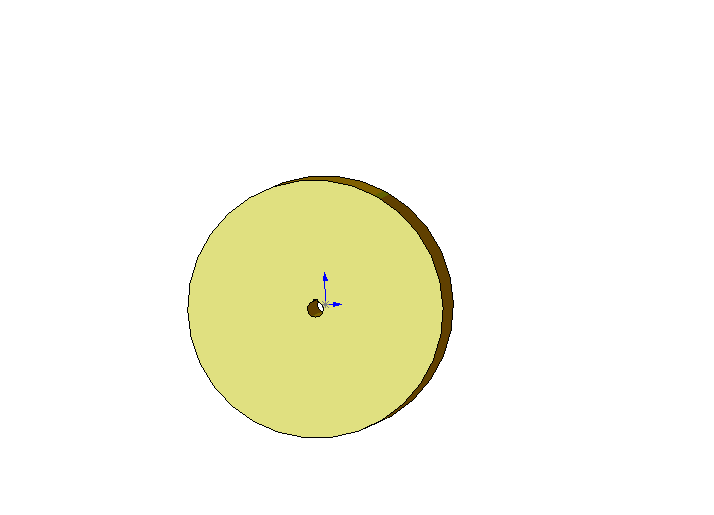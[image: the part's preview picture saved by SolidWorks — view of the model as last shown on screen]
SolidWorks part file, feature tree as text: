
SOLIDWORKS PART (.sldprt)
format: sldprt  version: not decoded by parser v0  size: 113,152 bytes
history: native  units: mm
features: sketch x3, cut_extrude x2, extrude x1 (+10 scaffold rows collapsed)
feature tree (16):
  scaffold x10  (default folders/planes/origin — collapsed)
  sketch  "Sketch1"  dims[D1=203.2mm]
  extrude  "Extrude1"  Depth=50.8mm
  sketch  "Sketch2"  dims[D1=12.7mm]
  cut_extrude  "Cut-Extrude1"  Depth=50.8mm
  sketch  "Sketch3"  dims[D1=3.175mm D2=3.175mm]
  cut_extrude  "Cut-Extrude2"  [1 undecoded]
decode coverage: 5 of 6 modeling features carry decoded parameters
note: 1 parameter value undecoded
note: suppression state not decoded; provenance and decode notes live in map.json
